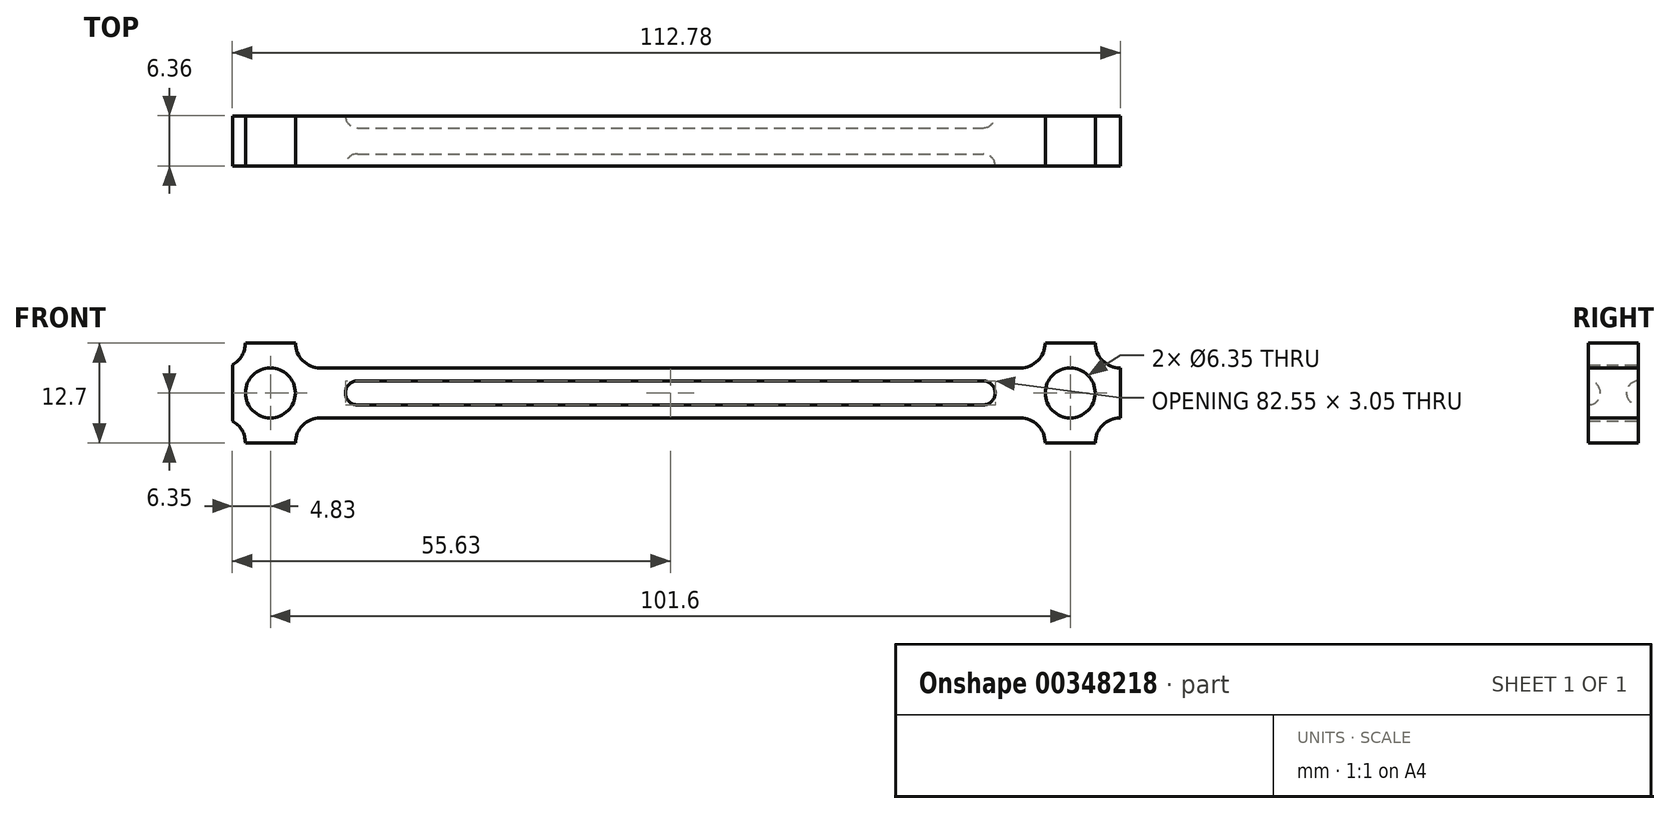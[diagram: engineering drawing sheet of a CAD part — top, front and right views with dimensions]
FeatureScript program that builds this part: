
annotation { "Feature Type Name" : "Feature", "Feature Type Description" : "" }
export const myFeature = defineFeature(function(context is Context, id is Id, definition is map)
    precondition{}
    {
        {
            var Q0;
            Q0=qCreatedBy(makeId("Front.planeOp"),FACE);
            var sketch = newSketch(context, id + "F0", { "sketchPlane" : qUnion([Q0])});
            skLineSegment(sketch, "E0", {"start": v(-44.45, 3.17) * mm, "end": v(44.45, 3.17) * mm});
            skArc(sketch, "E1", {"start": v(44.45, 3.17) * mm, "mid": v(46.7, 4.1) * mm, "end": v(47.63, 6.35) * mm});
            skLineSegment(sketch, "E2", {"start": v(47.62, 6.35) * mm, "end": v(53.98, 6.35) * mm});
            skLineSegment(sketch, "E3", {"start": v(57.15, 3.18) * mm, "end": v(57.15, -3.18) * mm});
            skLineSegment(sketch, "E4", {"start": v(53.98, -6.35) * mm, "end": v(47.62, -6.35) * mm});
            skLineSegment(sketch, "E5", {"start": v(44.45, -3.18) * mm, "end": v(-44.45, -3.18) * mm});
            skCircle(sketch, "E6", {"center": v(50.8, 0) * mm, "radius": 3.18 * mm});
            skCircle(sketch, "E7", {"center": v(-50.8, 0) * mm, "radius": 3.18 * mm});
            skPoint(sketch, "E8", {"position": v(0, 3.18) * mm});
            skPoint(sketch, "E9", {"position": v(57.15, 0) * mm});
            skArc(sketch, "E10", {"start": v(53.98, 6.35) * mm, "mid": v(54.9, 4.1) * mm, "end": v(57.15, 3.17) * mm});
            skPoint(sketch, "E11", {"position": v(50.8, 6.35) * mm});
            skPoint(sketch, "E12", {"position": v(50.8, -6.35) * mm});
            skArc(sketch, "E13", {"start": v(47.63, -6.35) * mm, "mid": v(46.7, -4.1) * mm, "end": v(44.45, -3.18) * mm});
            skArc(sketch, "E14", {"start": v(57.15, -3.17) * mm, "mid": v(54.9, -4.1) * mm, "end": v(53.98, -6.35) * mm});
            skArc(sketch, "E15", {"start": v(-47.62, 6.35) * mm, "mid": v(-46.7, 4.1) * mm, "end": v(-44.45, 3.18) * mm});
            skArc(sketch, "E16", {"start": v(-44.45, -3.18) * mm, "mid": v(-46.7, -4.1) * mm, "end": v(-47.62, -6.35) * mm});
            skLineSegment(sketch, "E17", {"start": v(-47.62, 6.35) * mm, "end": v(-53.97, 6.35) * mm});
            skLineSegment(sketch, "E18", {"start": v(-47.62, -6.35) * mm, "end": v(-53.97, -6.35) * mm});
            skArc(sketch, "E19", {"start": v(-55.63, 3.56) * mm, "mid": v(-54.42, 4.73) * mm, "end": v(-53.97, 6.35) * mm});
            skArc(sketch, "E20", {"start": v(-53.97, -6.35) * mm, "mid": v(-54.42, -4.73) * mm, "end": v(-55.63, -3.56) * mm});
            skPoint(sketch, "E21", {"position": v(-50.8, 6.35) * mm});
            skLineSegment(sketch, "E22", {"start": v(-55.63, 3.56) * mm, "end": v(-55.63, -3.56) * mm});
            skPoint(sketch, "E23.orphan", {"position": v(-57.15, 3.18) * mm});
            skPoint(sketch, "E24.orphan", {"position": v(-57.15, -3.18) * mm});
            skSolve(sketch);
        }
        {
            var Q0;
            Q0=qSketchRegion(id+"F0",true);
            extrude(context, id + "F1", {"entities" : qUnion([Q0]), "endBound" : BoundingType.SYMMETRIC, "depth" : 6.35 * mm});
        }
        {
            var Q0;
            Q0=qCreatedBy(makeId("Right.planeOp"),FACE);
            var sketch = newSketch(context, id + "F2", { "sketchPlane" : qUnion([Q0])});
            skArc(sketch, "E25", {"start": v(3.17, 1.52) * mm, "mid": v(1.65, 0) * mm, "end": v(3.18, -1.52) * mm});
            skArc(sketch, "E26", {"start": v(-3.18, -1.52) * mm, "mid": v(-1.65, 0) * mm, "end": v(-3.18, 1.52) * mm});
            skLineSegment(sketch, "E27", {"start": v(3.18, -1.52) * mm, "end": v(3.17, 1.52) * mm});
            skLineSegment(sketch, "E28", {"start": v(-3.18, -1.52) * mm, "end": v(-3.18, 1.52) * mm});
            skSolve(sketch);
        }
        {
            var Q0;
            Q0=qSketchRegion(id+"F2",true);
            extrude(context, id + "F3", {"entities" : qUnion([Q0]), "operationType" : NewBodyOperationType.REMOVE, "endBound" : BoundingType.SYMMETRIC, "oppositeDirection" : true, "depth" : 82.55 * mm});
        }
        {
            var Q0;
            Q0=makeQuery(id+"F3.boolean.opBoolean","COPY",EDGE,{"derivedFrom":makeQuery(id+"F3.opExtrude","CAP_EDGE",EDGE,{"disambiguationData":[OSD([sQuery(id+"F2.wireOp",EDGE,"E25")])],"isStart":true})});
            var Q1;
            Q1=makeQuery(id+"F3.boolean.opBoolean","COPY",EDGE,{"derivedFrom":makeQuery(id+"F3.opExtrude","CAP_EDGE",EDGE,{"disambiguationData":[OSD([sQuery(id+"F2.wireOp",EDGE,"E25")])],"isStart":false})});
            var Q2;
            Q2=makeQuery(id+"F3.boolean.opBoolean","COPY",EDGE,{"derivedFrom":makeQuery(id+"F3.opExtrude","CAP_EDGE",EDGE,{"disambiguationData":[OSD([sQuery(id+"F2.wireOp",EDGE,"E26")])],"isStart":false})});
            var Q3;
            Q3=makeQuery(id+"F3.boolean.opBoolean","COPY",EDGE,{"derivedFrom":makeQuery(id+"F3.opExtrude","CAP_EDGE",EDGE,{"disambiguationData":[OSD([sQuery(id+"F2.wireOp",EDGE,"E26")])],"isStart":true})});
            fillet(context, id + "F4", {"entities" : qUnion([Q0, Q1, Q2, Q3]), "radius" : 1.52 * mm, "tangentPropagation" : true, "allowEdgeOverflow" : false});
        }
    });
